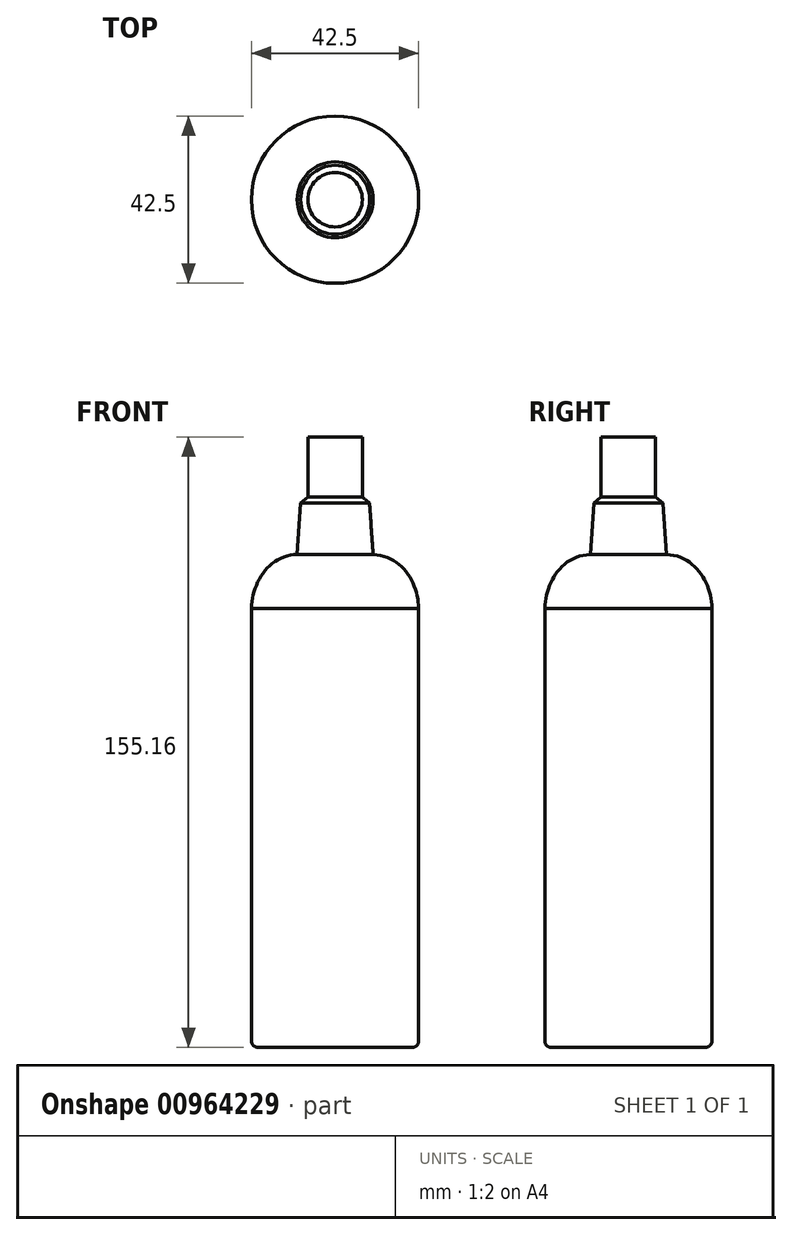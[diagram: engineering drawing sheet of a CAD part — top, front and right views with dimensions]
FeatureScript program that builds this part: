
annotation { "Feature Type Name" : "Feature", "Feature Type Description" : "" }
export const myFeature = defineFeature(function(context is Context, id is Id, definition is map)
    precondition{}
    {
        {
            var Q0;
            Q0=qCreatedBy(makeId("Front.planeOp"),FACE);
            var sketch = newSketch(context, id + "F0", { "sketchPlane" : qUnion([Q0])});
            skLineSegment(sketch, "E0", {"start": v(0, 0) * mm, "end": v(21.25, 0) * mm});
            skLineSegment(sketch, "E1", {"start": v(21.25, 0) * mm, "end": v(21.25, 111.6) * mm});
            skLineSegment(sketch, "E2", {"start": v(0, 155.16) * mm, "end": v(6.93, 155.16) * mm});
            skLineSegment(sketch, "E3", {"start": v(6.93, 155.16) * mm, "end": v(6.93, 139.86) * mm});
            skLineSegment(sketch, "E4", {"start": v(6.93, 139.86) * mm, "end": v(8.74, 138.38) * mm});
            skLineSegment(sketch, "E5", {"start": v(8.74, 138.38) * mm, "end": v(9.65, 125.26) * mm});
            skFitSpline(sketch, "E6", {"points": [v(9.65, 125.26) * mm, v(21.25, 111.6) * mm], "startDerivative": vector(22.98, -0.78) * mm, "endDerivative": vector(0.44, -17.97) * mm});
            skLineSegment(sketch, "E7", {"start": v(0, 155.16) * mm, "end": v(0, 0) * mm});
            skSolve(sketch);
        }
        {
            var Q0;
            Q0=makeQuery(id+"F0.imprint","IMPRINT",FACE,{"disambiguationData":[TD([[makeQuery(id+"F0.imprint","IMPRINT",EDGE,{"derivedFrom":sQuery(id+"F0.wireOp",EDGE,"E0")}),1.0]])]});
            var Q1;
            Q1=sQuery(id+"F0.wireOp",EDGE,"E7");
            revolve(context, id + "F1", {"surfaceOperationType" : NewSurfaceOperationType.NEW, "entities" : qUnion([Q0]), "axis" : qUnion([Q1]), "revolveType" : RevolveType.FULL});
        }
        {
            var Q0;
            Q0=makeQuery(id+"F1.opRevolve","SWEPT_EDGE",EDGE,{"disambiguationData":[OSD([sQuery(id+"F0.wireOp",EDGE,"E0"),sQuery(id+"F0.wireOp",EDGE,"E1")])]});
            fillet(context, id + "F2", {"entities" : qUnion([Q0]), "tangentPropagation" : true, "radius" : 1.69 * mm, "defaultsChanged" : false, "vertexSettings" : [], "allowEdgeOverflow" : false});
        }
    });
